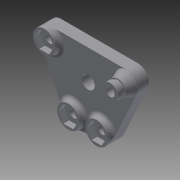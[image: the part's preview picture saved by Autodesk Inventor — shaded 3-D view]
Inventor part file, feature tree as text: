
AUTODESK INVENTOR PART (.ipt)
format: ipt  version: 2013 (Build 170138000, 138)  size: 241,664 bytes
history: native  units: in
note: dims shown in document units (in); Inventor stores cm internally (conversion verified against a paired STEP export)
features: extrude x6, sketch x6, fillet x2, draft x1
ambient origin geometry x8: Origin, YZ Plane, XZ Plane, XY Plane, X Axis, Y Axis, Z Axis, Center Point
bodies: Solid1 (feature_tree)
feature tree (15):
  extrude  "Extrusion1"  Depth=0.2953in
  extrude  "Extrusion2"  Depth=1.5433in
  fillet  "Fillet1"  Radius=0.1772in
  extrude  "Extrusion7"  Depth=1.7717in
  extrude  "Extrusion8"  Depth=0.7972in
  extrude  "Extrusion9"  Depth=0.1772in
  draft  "FaceDraft2"
  extrude  "Extrusion10"  Depth=0.2362in TaperAngle=0.0deg
  fillet  "Fillet3"  Radius=0.5118in
  sketch  "Sketch1"  dims[d0=0.2756in d1=0.2953in]
  sketch  "Sketch2"  dims[d2=0.2953in d3=1.5433in d4=0.1772in]
  sketch  "Sketch7"  dims[d5=0.1772in d6=1.7717in]
  sketch  "Sketch8"  dims[d7=0.7972in d8=0.7972in]
  sketch  "Sketch9"  dims[d9=0.1772in d10=0.1772in]
  sketch  "Sketch10"  dims[d11=0.2362in d12=0.2362in d13=0.0in d14=0.5118in d15=0.1772in d16=0.0in d17=0.1181in d27=0.4724in d28=0.2362in d29=0.4724in d30=0.4724in d38=0.3248in d39=0.1772in d40=0.0in d41=0.2756in d42=0.0591in d43=0.0in d44=0.3248in d45=0.0984in d46=0.0in d47=0.1512in d48=0.3543in d49=0.3543in d50=0.3543in d51=0.1181in d52=0.0in d53=0.0787in]
